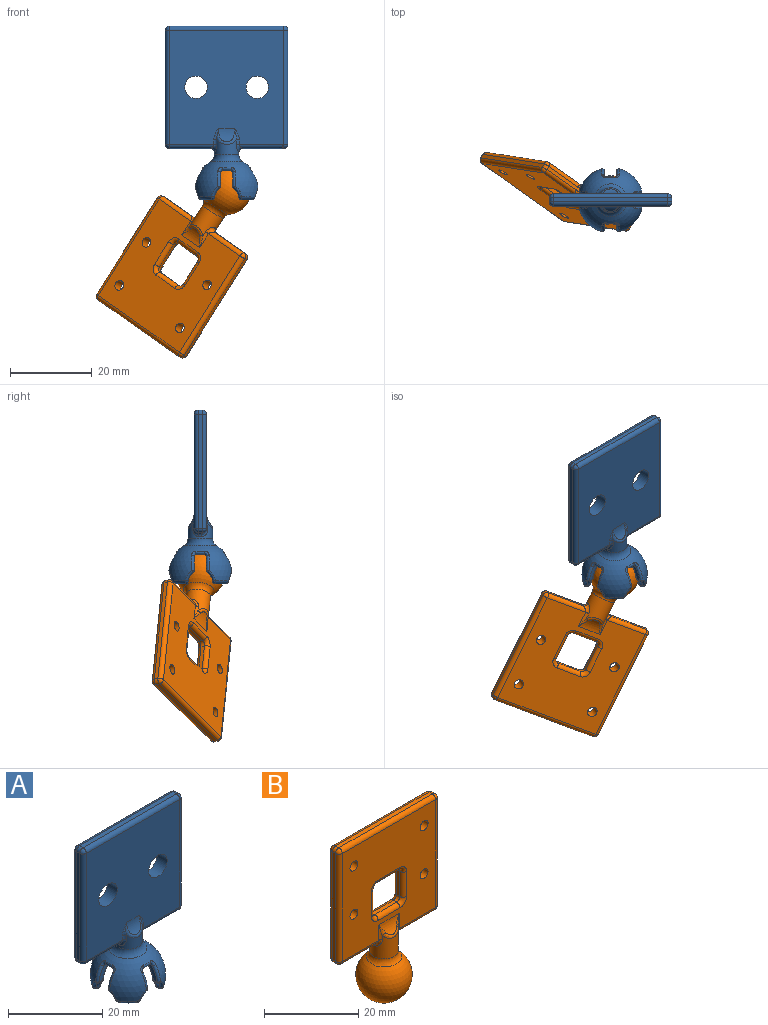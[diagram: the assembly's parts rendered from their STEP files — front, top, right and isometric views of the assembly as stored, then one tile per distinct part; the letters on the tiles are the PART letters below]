
ASSEMBLY  parts=2 mates=1
PART A: 173 faces, bbox 30x16.6x42.7 mm
  f0: torus R=6.87mm, axis (0,0,1), area 10.6mm2, adj f4,f5,f112,f133
  f1: torus R=6.87mm, axis (0,0,1), area 10.6mm2, adj f4,f5,f93,f113
  f2: torus R=6.87mm, axis (0,0,1), area 10.6mm2, adj f4,f5,f132,f153
  f3: cylinder r=3mm len=6mm, axis (0,0,1), area 38.5mm2, adj f17,f27,f34,f35,f40,f45,f46,f48
  f4: sphere r=8mm, area 274.4mm2, adj f0,f1,f2,f17,f18,f94,f98,f100
  f5: sphere r=6mm, area 154.3mm2, adj f0,f1,f2,f18,f95,f99,f101,f103
  f6: plane 10.03x1mm, normal (0,0,-1), area 10mm2, adj f28,f29,f40,f41
  f7: plane 10.03x1mm, normal (0,0,-1), area 10mm2, adj f43,f44,f50,f51
  f8: plane 28x1mm, normal (1,0,0), area 28mm2, adj f32,f33,f42,f43
  f9: plane 28x1mm, normal (0,0,1), area 28mm2, adj f21,f22,f31,f32
  f10: cylinder r=2.75mm len=5.5mm, axis (0,1,0), area 51.8mm2, adj f13,f14
  f11: plane 28x1mm, normal (-1,0,0), area 28mm2, adj f20,f21,f29,f30
  f12: cylinder r=2.75mm len=5.5mm, axis (0,1,0), area 51.8mm2, adj f13,f14
  f13: plane 28x28mm, normal (0,-1,0), area 713.9mm2, adj f10,f12,f16,f30,f31,f41,f42,f49
  f14: plane 28x28mm, normal (0,1,0), area 713.9mm2, adj f10,f12,f15,f20,f22,f26,f27,f28
  f15: cylinder r=5mm len=3.87mm, axis (-1,0,0), area 11.7mm2, adj f14,f34
  f16: cylinder r=5mm len=3.87mm, axis (1,0,0), area 11.7mm2, adj f13,f54
  f17: torus R=5mm, axis (0,0,-1), area 44mm2, adj f3,f4
  f18: torus R=6.87mm, axis (0,0,1), area 10.6mm2, adj f4,f5,f152,f172
  f19: sphere r=1mm, area 1.6mm2, adj f20,f21,f22
  f20: cylinder r=1mm len=28mm, axis (0,0,-1), area 44mm2, adj f11,f14,f19,f23
  f21: cylinder r=1mm len=1mm, axis (0,-1,0), area 1.6mm2, adj f9,f11,f19,f24
  f22: cylinder r=1mm len=28mm, axis (-1,0,0), area 44mm2, adj f9,f14,f19,f25
  f23: sphere r=1mm, area 0.9mm2, adj f20,f28,f29
  f24: sphere r=1mm, area 1.6mm2, adj f21,f30,f31
  f25: sphere r=1mm, area 1mm2, adj f22,f32,f33
  f26: bspline ~3.55x1.19mm, area 1mm2, adj f14,f27,f34
  f27: cylinder r=1mm len=1.1mm, axis (0,0,1), area 1mm2, adj f3,f14,f26,f35
  f28: cylinder r=1mm len=10.88mm, axis (1,0,0), area 16.4mm2, adj f6,f14,f23,f35
  f29: cylinder r=1mm len=1mm, axis (0,1,0), area 1.6mm2, adj f6,f11,f23,f36
  f30: cylinder r=1mm len=28mm, axis (0,0,1), area 44mm2, adj f11,f13,f24,f36
  f31: cylinder r=1mm len=28mm, axis (1,0,0), area 44mm2, adj f9,f13,f24,f37
  f32: cylinder r=1mm len=1mm, axis (0,1,0), area 1.6mm2, adj f8,f9,f25,f37
  f33: cylinder r=1mm len=28mm, axis (0,0,1), area 44mm2, adj f8,f14,f25,f38
  f34: bspline ~5.81x4.49mm, area 7.3mm2, adj f3,f15,f26,f39
  f35: bspline ~2.17x1.8mm, area 2.6mm2, adj f3,f27,f28,f40
  f36: sphere r=1mm, area 1.6mm2, adj f29,f30,f41
  f37: sphere r=1mm, area 1.6mm2, adj f31,f32,f42
  f38: sphere r=1mm, area 1.6mm2, adj f33,f43,f44
  f39: bspline ~2.9x1.19mm, area 1mm2, adj f14,f34,f45
  f40: torus R=4mm, axis (0,0,1), area 1.3mm2, adj f3,f6,f35,f46
  f41: cylinder r=1mm len=10.88mm, axis (-1,0,0), area 16.4mm2, adj f6,f13,f36,f46
  f42: cylinder r=1mm len=28mm, axis (0,0,-1), area 44mm2, adj f8,f13,f37,f47
  f43: cylinder r=1mm len=1mm, axis (0,-1,0), area 1.6mm2, adj f7,f8,f38,f47
  f44: cylinder r=1mm len=10.88mm, axis (1,0,0), area 16.4mm2, adj f7,f14,f38,f48
  f45: cylinder r=1mm len=1.1mm, axis (0,0,1), area 1mm2, adj f3,f14,f39,f48
  f46: bspline ~2.38x1.65mm, area 2.6mm2, adj f3,f40,f41,f49
  f47: sphere r=1mm, area 2.1mm2, adj f42,f43,f50
  f48: bspline ~2.38x1.65mm, area 2.6mm2, adj f3,f44,f45,f51
  f49: cylinder r=1mm len=1.1mm, axis (0,0,1), area 1mm2, adj f3,f13,f46,f52
  f50: cylinder r=1mm len=10.88mm, axis (-1,0,0), area 16.4mm2, adj f7,f13,f47,f53
  f51: torus R=4mm, axis (0,0,1), area 1.3mm2, adj f3,f7,f48,f53
  f52: bspline ~3.55x1.19mm, area 1mm2, adj f13,f49,f54
  f53: bspline ~2.17x1.8mm, area 2.6mm2, adj f3,f50,f51,f55
  f54: bspline ~5.81x4.49mm, area 7.3mm2, adj f3,f16,f52,f56
  f55: cylinder r=1mm len=1.1mm, axis (0,0,1), area 1mm2, adj f3,f13,f53,f56
  f56: bspline ~2.9x1.19mm, area 1mm2, adj f13,f54,f55
  f57: cylinder r=3mm len=2.35mm, axis (0,1,0), area 3mm2, adj f60,f170,f171,f172
  f58: plane 3.42x2.72mm, normal (-1,0,0), area 4mm2, adj f59,f60,f166,f167
  f59: cylinder r=0.5mm len=2.18mm, axis (0,1,0), area 1.2mm2, adj f58,f65,f164,f165
  f60: cylinder r=0.5mm len=1.05mm, axis (0,1,0), area 0.5mm2, adj f57,f58,f168,f169
  f61: cylinder r=0.5mm len=2.18mm, axis (0,1,0), area 1.2mm2, adj f62,f65,f160,f161
  f62: plane 3.42x2.72mm, normal (1,0,0), area 4mm2, adj f61,f64,f158,f159
  f63: cylinder r=3mm len=2.35mm, axis (0,1,0), area 3mm2, adj f64,f153,f154,f155
  f64: cylinder r=0.5mm len=1.05mm, axis (0,1,0), area 0.5mm2, adj f62,f63,f156,f157
  f65: plane 2x1.68mm, normal (0,0,-1), area 3.1mm2, adj f59,f61,f162,f163
  f66: cylinder r=3mm len=2.35mm, axis (-1,0,0), area 3mm2, adj f69,f133,f134,f135
  f67: plane 3.42x2.72mm, normal (0,-1,0), area 4mm2, adj f68,f69,f138,f139
  f68: cylinder r=0.5mm len=2.18mm, axis (-1,0,0), area 1.2mm2, adj f67,f74,f140,f141
  f69: cylinder r=0.5mm len=1.05mm, axis (-1,0,0), area 0.5mm2, adj f66,f67,f136,f137
  f70: cylinder r=0.5mm len=2.18mm, axis (-1,0,0), area 1.2mm2, adj f71,f74,f144,f145
  f71: plane 3.42x2.72mm, normal (0,1,0), area 4mm2, adj f70,f73,f146,f147
  f72: cylinder r=3mm len=2.35mm, axis (-1,0,0), area 3mm2, adj f73,f150,f151,f152
  f73: cylinder r=0.5mm len=1.05mm, axis (-1,0,0), area 0.5mm2, adj f71,f72,f148,f149
  f74: plane 2x1.68mm, normal (0,0,-1), area 3.1mm2, adj f68,f70,f142,f143
  f75: cylinder r=3mm len=2.35mm, axis (-1,0,0), area 3mm2, adj f78,f130,f131,f132
  f76: plane 3.42x2.72mm, normal (0,1,0), area 4mm2, adj f77,f78,f126,f127
  f77: cylinder r=0.5mm len=2.18mm, axis (1,0,0), area 1.2mm2, adj f76,f83,f124,f125
  f78: cylinder r=0.5mm len=1.05mm, axis (1,0,0), area 0.5mm2, adj f75,f76,f128,f129
  f79: plane 3.42x2.72mm, normal (0,-1,0), area 4mm2, adj f80,f82,f118,f119
  f80: cylinder r=0.5mm len=2.18mm, axis (-1,0,0), area 1.2mm2, adj f79,f83,f120,f121
  f81: cylinder r=3mm len=2.35mm, axis (-1,0,0), area 3mm2, adj f82,f113,f114,f115
  f82: cylinder r=0.5mm len=1.05mm, axis (-1,0,0), area 0.5mm2, adj f79,f81,f116,f117
  f83: plane 2x1.68mm, normal (0,0,-1), area 3.1mm2, adj f77,f80,f122,f123
  f84: plane 3.42x2.72mm, normal (1,0,0), area 4mm2, adj f85,f89,f98,f99
  f85: cylinder r=0.5mm len=1.05mm, axis (0,-1,0), area 0.5mm2, adj f84,f92,f96,f97
  f86: cylinder r=0.5mm len=1.05mm, axis (0,-1,0), area 0.5mm2, adj f87,f91,f108,f109
  f87: plane 3.42x2.72mm, normal (-1,0,0), area 4mm2, adj f86,f90,f106,f107
  f88: plane 2x1.68mm, normal (0,0,-1), area 3.1mm2, adj f89,f90,f102,f103
  f89: cylinder r=0.5mm len=2.18mm, axis (0,-1,0), area 1.2mm2, adj f84,f88,f100,f101
  f90: cylinder r=0.5mm len=2.18mm, axis (0,-1,0), area 1.2mm2, adj f87,f88,f104,f105
  f91: cylinder r=3mm len=2.35mm, axis (0,-1,0), area 3mm2, adj f86,f110,f111,f112
  f92: cylinder r=3mm len=2.35mm, axis (0,-1,0), area 3mm2, adj f85,f93,f94,f95
  f93: bspline ~2.4x1.3mm, area 1.9mm2, adj f1,f92,f94,f95
  f94: bspline ~3.28x2.58mm, area 2.6mm2, adj f4,f92,f93,f96
  f95: bspline ~3.24x2.13mm, area 1.4mm2, adj f5,f92,f93,f97
  f96: sphere r=0.5mm, area 0.3mm2, adj f85,f94,f98
  f97: sphere r=0.5mm, area 0.2mm2, adj f85,f95,f99
  f98: torus R=7.23mm, axis (1,0,0), area 3.6mm2, adj f4,f84,f96,f100
  f99: torus R=6.18mm, axis (1,0,0), area 2.3mm2, adj f5,f84,f97,f101
  f100: bspline ~1.49x1.29mm, area 1.3mm2, adj f4,f89,f98,f102
  f101: bspline ~1.18x0.98mm, area 0.6mm2, adj f5,f89,f99,f103
  f102: torus R=5.31mm, axis (0,0,-1), area 2.5mm2, adj f4,f88,f100,f104
  f103: torus R=3.77mm, axis (0,0,-1), area 0.6mm2, adj f5,f88,f101,f105
  f104: bspline ~1.49x1.27mm, area 1.3mm2, adj f4,f90,f102,f106
  f105: bspline ~1.2x1.11mm, area 0.6mm2, adj f5,f90,f103,f107
  f106: torus R=7.23mm, axis (1,0,0), area 3.6mm2, adj f4,f87,f104,f108
  f107: torus R=6.18mm, axis (1,0,0), area 2.3mm2, adj f5,f87,f105,f109
  f108: sphere r=0.5mm, area 0.3mm2, adj f86,f106,f110
  f109: sphere r=0.5mm, area 0.2mm2, adj f86,f107,f111
  f110: bspline ~3.28x2.58mm, area 2.6mm2, adj f4,f91,f108,f112
  f111: bspline ~3.24x2.13mm, area 1.4mm2, adj f5,f91,f109,f112
  f112: bspline ~2.4x1.3mm, area 1.9mm2, adj f0,f91,f110,f111
  f113: bspline ~2.4x1.3mm, area 1.9mm2, adj f1,f81,f114,f115
  f114: bspline ~3.24x2.13mm, area 1.4mm2, adj f5,f81,f113,f116
  f115: bspline ~3.28x2.58mm, area 2.6mm2, adj f4,f81,f113,f117
  f116: sphere r=0.5mm, area 0.2mm2, adj f82,f114,f118
  f117: sphere r=0.5mm, area 0.3mm2, adj f82,f115,f119
  f118: torus R=6.18mm, axis (0,-1,0), area 2.3mm2, adj f5,f79,f116,f120
  f119: torus R=7.23mm, axis (0,-1,0), area 3.6mm2, adj f4,f79,f117,f121
  f120: bspline ~1.42x1.2mm, area 0.6mm2, adj f5,f80,f118,f122
  f121: bspline ~1.39x1.29mm, area 1.3mm2, adj f4,f80,f119,f123
  f122: torus R=3.77mm, axis (0,0,-1), area 0.6mm2, adj f5,f83,f120,f124
  f123: torus R=5.31mm, axis (0,0,-1), area 2.5mm2, adj f4,f83,f121,f125
  f124: bspline ~1.18x0.98mm, area 0.6mm2, adj f5,f77,f122,f126
  f125: bspline ~1.49x1.29mm, area 1.3mm2, adj f4,f77,f123,f127
  f126: torus R=6.18mm, axis (0,1,0), area 2.3mm2, adj f5,f76,f124,f128
  f127: torus R=7.23mm, axis (0,1,0), area 3.6mm2, adj f4,f76,f125,f129
  f128: sphere r=0.5mm, area 0.2mm2, adj f78,f126,f130
  f129: sphere r=0.5mm, area 0.3mm2, adj f78,f127,f131
  f130: bspline ~3.24x2.13mm, area 1.4mm2, adj f5,f75,f128,f132
  f131: bspline ~3.28x2.58mm, area 2.6mm2, adj f4,f75,f129,f132
  f132: bspline ~2.4x1.46mm, area 1.9mm2, adj f2,f75,f130,f131
  f133: bspline ~2.4x1.3mm, area 1.9mm2, adj f0,f66,f134,f135
  f134: bspline ~3.83x2.59mm, area 2.6mm2, adj f4,f66,f133,f136
  f135: bspline ~3.24x2.13mm, area 1.4mm2, adj f5,f66,f133,f137
  f136: sphere r=0.5mm, area 0.3mm2, adj f69,f134,f138
  f137: sphere r=0.5mm, area 0.2mm2, adj f69,f135,f139
  f138: torus R=7.23mm, axis (0,-1,0), area 3.6mm2, adj f4,f67,f136,f140
  f139: torus R=6.18mm, axis (0,-1,0), area 2.3mm2, adj f5,f67,f137,f141
  f140: bspline ~1.49x1.29mm, area 1.3mm2, adj f4,f68,f138,f142
  f141: bspline ~1.18x0.98mm, area 0.6mm2, adj f5,f68,f139,f143
  f142: torus R=5.31mm, axis (0,0,-1), area 2.5mm2, adj f4,f74,f140,f144
  f143: torus R=3.77mm, axis (0,0,-1), area 0.6mm2, adj f5,f74,f141,f145
  f144: bspline ~1.39x1.29mm, area 1.3mm2, adj f4,f70,f142,f146
  f145: bspline ~1.42x1.2mm, area 0.6mm2, adj f5,f70,f143,f147
  f146: torus R=7.23mm, axis (0,-1,0), area 3.6mm2, adj f4,f71,f144,f148
  f147: torus R=6.18mm, axis (0,-1,0), area 2.3mm2, adj f5,f71,f145,f149
  f148: sphere r=0.5mm, area 0.3mm2, adj f73,f146,f150
  f149: sphere r=0.5mm, area 0.2mm2, adj f73,f147,f151
  f150: bspline ~3.28x2.58mm, area 2.6mm2, adj f4,f72,f148,f152
  f151: bspline ~3.24x2.13mm, area 1.4mm2, adj f5,f72,f149,f152
  f152: bspline ~2.4x1.3mm, area 1.9mm2, adj f18,f72,f150,f151
  f153: bspline ~2.4x1.3mm, area 1.9mm2, adj f2,f63,f154,f155
  f154: bspline ~3.24x2.13mm, area 1.4mm2, adj f5,f63,f153,f156
  f155: bspline ~3.28x2.58mm, area 2.6mm2, adj f4,f63,f153,f157
  f156: sphere r=0.5mm, area 0.2mm2, adj f64,f154,f158
  f157: sphere r=0.5mm, area 0.3mm2, adj f64,f155,f159
  f158: torus R=6.18mm, axis (-1,0,0), area 2.3mm2, adj f5,f62,f156,f160
  f159: torus R=7.23mm, axis (-1,0,0), area 3.6mm2, adj f4,f62,f157,f161
  f160: bspline ~1.42x1.2mm, area 0.6mm2, adj f5,f61,f158,f162
  f161: bspline ~1.39x1.29mm, area 1.3mm2, adj f4,f61,f159,f163
  f162: torus R=3.77mm, axis (0,0,-1), area 0.6mm2, adj f5,f65,f160,f164
  f163: torus R=5.31mm, axis (0,0,-1), area 2.5mm2, adj f4,f65,f161,f165
  f164: bspline ~1.18x0.98mm, area 0.6mm2, adj f5,f59,f162,f166
  f165: bspline ~1.49x1.29mm, area 1.3mm2, adj f4,f59,f163,f167
  f166: torus R=6.18mm, axis (-1,0,0), area 2.3mm2, adj f5,f58,f164,f168
  f167: torus R=7.23mm, axis (-1,0,0), area 3.6mm2, adj f4,f58,f165,f169
  f168: sphere r=0.5mm, area 0.2mm2, adj f60,f166,f170
  f169: sphere r=0.5mm, area 0.3mm2, adj f60,f167,f171
  f170: bspline ~3.24x2.13mm, area 1.4mm2, adj f5,f57,f168,f172
  f171: bspline ~3.83x2.59mm, area 2.6mm2, adj f4,f57,f169,f172
  f172: bspline ~2.4x1.3mm, area 1.9mm2, adj f18,f57,f170,f171
PART B: 78 faces, bbox 30x12x46.2 mm
  f0: plane 28x28mm, normal (0,1,0), area 634.1mm2, adj f13,f14,f15,f16,f17,f20,f22,f27
  f1: plane 28x28mm, normal (0,-1,0), area 634.1mm2, adj f13,f14,f15,f16,f18,f24,f29,f34
  f2: cylinder r=3mm len=6.05mm, axis (0,0,1), area 84.1mm2, adj f19,f20,f21,f23,f24,f26,f42,f46
  f3: sphere r=6mm, area 402.8mm2, adj f19
  f4: plane 10.03x1mm, normal (0,0,-1), area 10mm2, adj f43,f44,f48,f49
  f5: plane 10.03x1mm, normal (0,0,-1), area 10mm2, adj f22,f23,f28,f29
  f6: plane 28x1mm, normal (1,0,0), area 28mm2, adj f27,f28,f33,f34
  f7: plane 28x1mm, normal (0,0,1), area 28mm2, adj f32,f33,f38,f39
  f8: plane 6.5x1mm, normal (0,0,1), area 6.5mm2, adj f58,f59,f67,f68
  f9: plane 6.5x1mm, normal (1,0,0), area 6.5mm2, adj f57,f66,f67,f71
  f10: plane 6.5x1mm, normal (0,0,-1), area 6.5mm2, adj f55,f56,f65,f66
  f11: plane 28x1mm, normal (-1,0,0), area 28mm2, adj f37,f38,f44,f45
  f12: plane 6.5x1mm, normal (-1,0,0), area 6.5mm2, adj f52,f55,f59,f60
  f13: cylinder r=1.2mm len=3mm, axis (0,1,0), area 22.6mm2, adj f0,f1
  f14: cylinder r=1.2mm len=3mm, axis (0,1,0), area 22.6mm2, adj f0,f1
  f15: cylinder r=1.2mm len=3mm, axis (0,1,0), area 22.6mm2, adj f0,f1
  f16: cylinder r=1.2mm len=3mm, axis (0,1,0), area 22.6mm2, adj f0,f1
  f17: cylinder r=5mm len=6.25mm, axis (-1,0,0), area 14mm2, adj f0,f75,f76,f77
  f18: cylinder r=5mm len=6.25mm, axis (1,0,0), area 14mm2, adj f1,f72,f73,f74
  f19: torus R=5mm, axis (0,0,-1), area 36.7mm2, adj f2,f3
  f20: cylinder r=1mm len=4mm, axis (0,0,1), area 2.3mm2, adj f0,f2,f21,f75
  f21: bspline ~2.38x1.65mm, area 2.6mm2, adj f2,f20,f22,f23
  f22: cylinder r=1mm len=10.88mm, axis (1,0,0), area 16.5mm2, adj f0,f5,f21,f25
  f23: torus R=4mm, axis (0,0,-1), area 1.3mm2, adj f2,f5,f21,f26
  f24: cylinder r=1mm len=4mm, axis (0,0,1), area 2.3mm2, adj f1,f2,f26,f74
  f25: sphere r=1mm, area 1.6mm2, adj f22,f27,f28
  f26: bspline ~2.17x1.8mm, area 2.6mm2, adj f2,f23,f24,f29
  f27: cylinder r=1mm len=28mm, axis (0,0,1), area 44mm2, adj f0,f6,f25,f30
  f28: cylinder r=1mm len=1mm, axis (0,1,0), area 1.6mm2, adj f5,f6,f25,f31
  f29: cylinder r=1mm len=10.88mm, axis (-1,0,0), area 16.5mm2, adj f1,f5,f26,f31
  f30: sphere r=1mm, area 1.6mm2, adj f27,f32,f33
  f31: sphere r=1mm, area 1.6mm2, adj f28,f29,f34
  f32: cylinder r=1mm len=28mm, axis (-1,0,0), area 44mm2, adj f0,f7,f30,f35
  f33: cylinder r=1mm len=1mm, axis (0,1,0), area 1.6mm2, adj f6,f7,f30,f36
  f34: cylinder r=1mm len=28mm, axis (0,0,-1), area 44mm2, adj f1,f6,f31,f36
  f35: sphere r=1mm, area 1.6mm2, adj f32,f37,f38
  f36: sphere r=1mm, area 1.6mm2, adj f33,f34,f39
  f37: cylinder r=1mm len=28mm, axis (0,0,-1), area 44mm2, adj f0,f11,f35,f40
  f38: cylinder r=1mm len=1mm, axis (0,-1,0), area 1.6mm2, adj f7,f11,f35,f41
  f39: cylinder r=1mm len=28mm, axis (1,0,0), area 44mm2, adj f1,f7,f36,f41
  f40: sphere r=1mm, area 1.6mm2, adj f37,f43,f44
  f41: sphere r=1mm, area 1.6mm2, adj f38,f39,f45
  f42: cylinder r=1mm len=4mm, axis (0,0,1), area 2.3mm2, adj f0,f2,f46,f77
  f43: cylinder r=1mm len=10.88mm, axis (1,0,0), area 16.5mm2, adj f0,f4,f40,f46
  f44: cylinder r=1mm len=1mm, axis (0,-1,0), area 1.6mm2, adj f4,f11,f40,f47
  f45: cylinder r=1mm len=28mm, axis (0,0,1), area 44mm2, adj f1,f11,f41,f47
  f46: bspline ~2.17x1.8mm, area 2.6mm2, adj f2,f42,f43,f48
  f47: sphere r=1mm, area 1.6mm2, adj f44,f45,f49
  f48: torus R=4mm, axis (0,0,-1), area 1.3mm2, adj f2,f4,f46,f50
  f49: cylinder r=1mm len=10.88mm, axis (-1,0,0), area 16.5mm2, adj f1,f4,f47,f50
  f50: bspline ~2.38x1.65mm, area 2.6mm2, adj f2,f48,f49,f51
  f51: cylinder r=1mm len=4mm, axis (0,0,1), area 2.3mm2, adj f1,f2,f50,f72
  f52: cylinder r=1mm len=6.5mm, axis (0,0,-1), area 10.2mm2, adj f0,f12,f53,f54
  f53: torus R=2mm, axis (0,-1,0), area 3.4mm2, adj f0,f52,f55,f56
  f54: torus R=2mm, axis (0,-1,0), area 3.4mm2, adj f0,f52,f58,f59
  f55: cylinder r=1mm len=1mm, axis (0,-1,0), area 1.6mm2, adj f10,f12,f53,f61
  f56: cylinder r=1mm len=6.5mm, axis (1,0,0), area 10.2mm2, adj f0,f10,f53,f62
  f57: cylinder r=1mm len=6.5mm, axis (0,0,1), area 10.2mm2, adj f0,f9,f62,f63
  f58: cylinder r=1mm len=6.5mm, axis (-1,0,0), area 10.2mm2, adj f0,f8,f54,f63
  f59: cylinder r=1mm len=1mm, axis (0,1,0), area 1.6mm2, adj f8,f12,f54,f64
  f60: cylinder r=1mm len=6.5mm, axis (0,0,1), area 10.2mm2, adj f1,f12,f61,f64
  f61: torus R=2mm, axis (0,-1,0), area 3.4mm2, adj f1,f55,f60,f65
  f62: torus R=2mm, axis (0,-1,0), area 3.4mm2, adj f0,f56,f57,f66
  f63: torus R=2mm, axis (0,-1,0), area 3.4mm2, adj f0,f57,f58,f67
  f64: torus R=2mm, axis (0,-1,0), area 3.4mm2, adj f1,f59,f60,f68
  f65: cylinder r=1mm len=6.5mm, axis (-1,0,0), area 10.2mm2, adj f1,f10,f61,f69
  f66: cylinder r=1mm len=1mm, axis (0,1,0), area 1.6mm2, adj f9,f10,f62,f69
  f67: cylinder r=1mm len=1mm, axis (0,-1,0), area 1.6mm2, adj f8,f9,f63,f70
  f68: cylinder r=1mm len=6.5mm, axis (1,0,0), area 10.2mm2, adj f1,f8,f64,f70
  f69: torus R=2mm, axis (0,-1,0), area 3.4mm2, adj f1,f65,f66,f71
  f70: torus R=2mm, axis (0,-1,0), area 3.4mm2, adj f1,f67,f68,f71
  f71: cylinder r=1mm len=6.5mm, axis (0,0,-1), area 10.2mm2, adj f1,f9,f69,f70
  f72: bspline ~2.9x1.56mm, area 1.4mm2, adj f18,f51,f73
  f73: bspline ~4.94x1.85mm, area 4.1mm2, adj f2,f18,f72,f74
  f74: bspline ~2.9x1.56mm, area 1.4mm2, adj f18,f24,f73
  f75: bspline ~2.9x1.56mm, area 1.4mm2, adj f17,f20,f76
  f76: bspline ~5.08x1.85mm, area 4.1mm2, adj f2,f17,f75,f77
  f77: bspline ~3.06x1.63mm, area 1.4mm2, adj f17,f42,f76
PLACE A t=(-29.72,-0.59,3.94)mm fixed
PLACE B rot(axis=(-0.27,-0.96,0.03),147.7deg) t=(-70.42,29.8,-26.22)mm
MATE ball B.f2 <-> A.f0  axis (-0.53,0.08,-0.84) through (-14.72,-0.59,-27.28)mm
